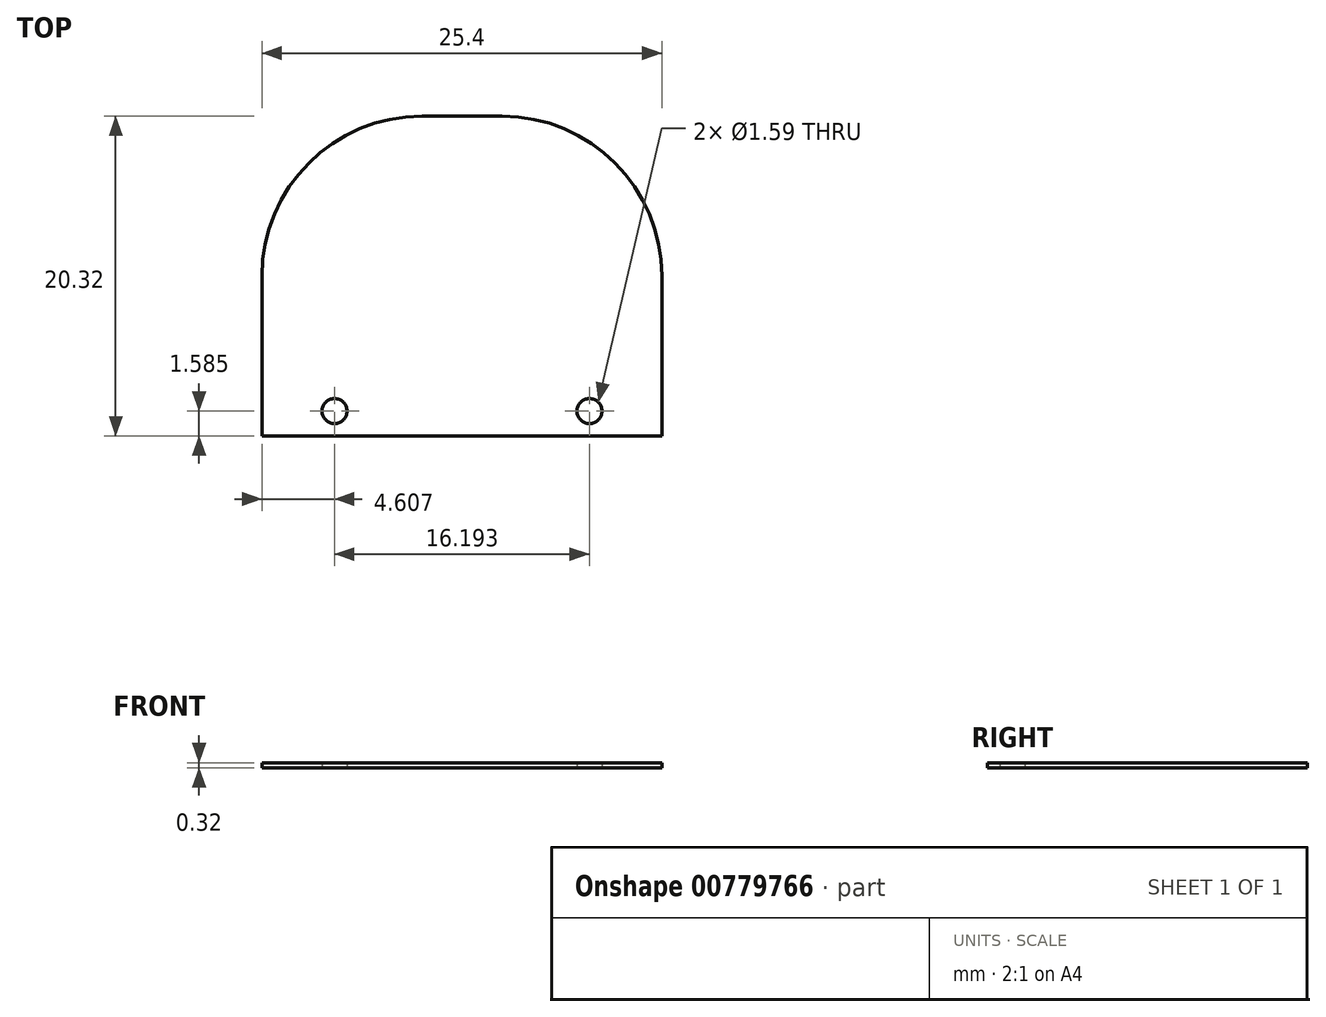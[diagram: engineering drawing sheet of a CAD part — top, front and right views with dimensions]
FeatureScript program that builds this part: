
annotation { "Feature Type Name" : "Feature", "Feature Type Description" : "" }
export const myFeature = defineFeature(function(context is Context, id is Id, definition is map)
    precondition{}
    {
        {
            var Q0;
            Q0=qCreatedBy(makeId("Top.planeOp"),FACE);
            var sketch = newSketch(context, id + "F0", { "sketchPlane" : qUnion([Q0])});
            skLineSegment(sketch, "E0", {"start": v(-14.14, 0.09) * mm, "end": v(-14.14, -10.07) * mm});
            skLineSegment(sketch, "E1", {"start": v(-14.14, -10.07) * mm, "end": v(11.26, -10.07) * mm});
            skLineSegment(sketch, "E2", {"start": v(11.26, -10.07) * mm, "end": v(11.26, 0.09) * mm});
            skArc(sketch, "E3", {"start": v(-3.98, 10.25) * mm, "mid": v(-11.16, 7.27) * mm, "end": v(-14.14, 0.09) * mm});
            skArc(sketch, "E4", {"start": v(11.26, 0.09) * mm, "mid": v(8.29, 7.27) * mm, "end": v(1.1, 10.25) * mm});
            skLineSegment(sketch, "E5", {"start": v(-3.98, 10.25) * mm, "end": v(1.1, 10.25) * mm});
            skCircle(sketch, "E6", {"center": v(-9.53, -8.48) * mm, "radius": 0.8 * mm});
            skCircle(sketch, "E7", {"center": v(6.66, -8.48) * mm, "radius": 0.8 * mm});
            skSolve(sketch);
        }
        {
            var Q0;
            Q0=makeQuery(id+"F0.imprint","IMPRINT",FACE,{"disambiguationData":[TD([[makeQuery(id+"F0.imprint","IMPRINT",EDGE,{"derivedFrom":sQuery(id+"F0.wireOp",EDGE,"E0")}),1.0]])]});
            extrude(context, id + "F1", {"entities" : qUnion([Q0]), "depth" : 0.32 * mm, "offsetDistance" : 25.4 * mm});
        }
    });
